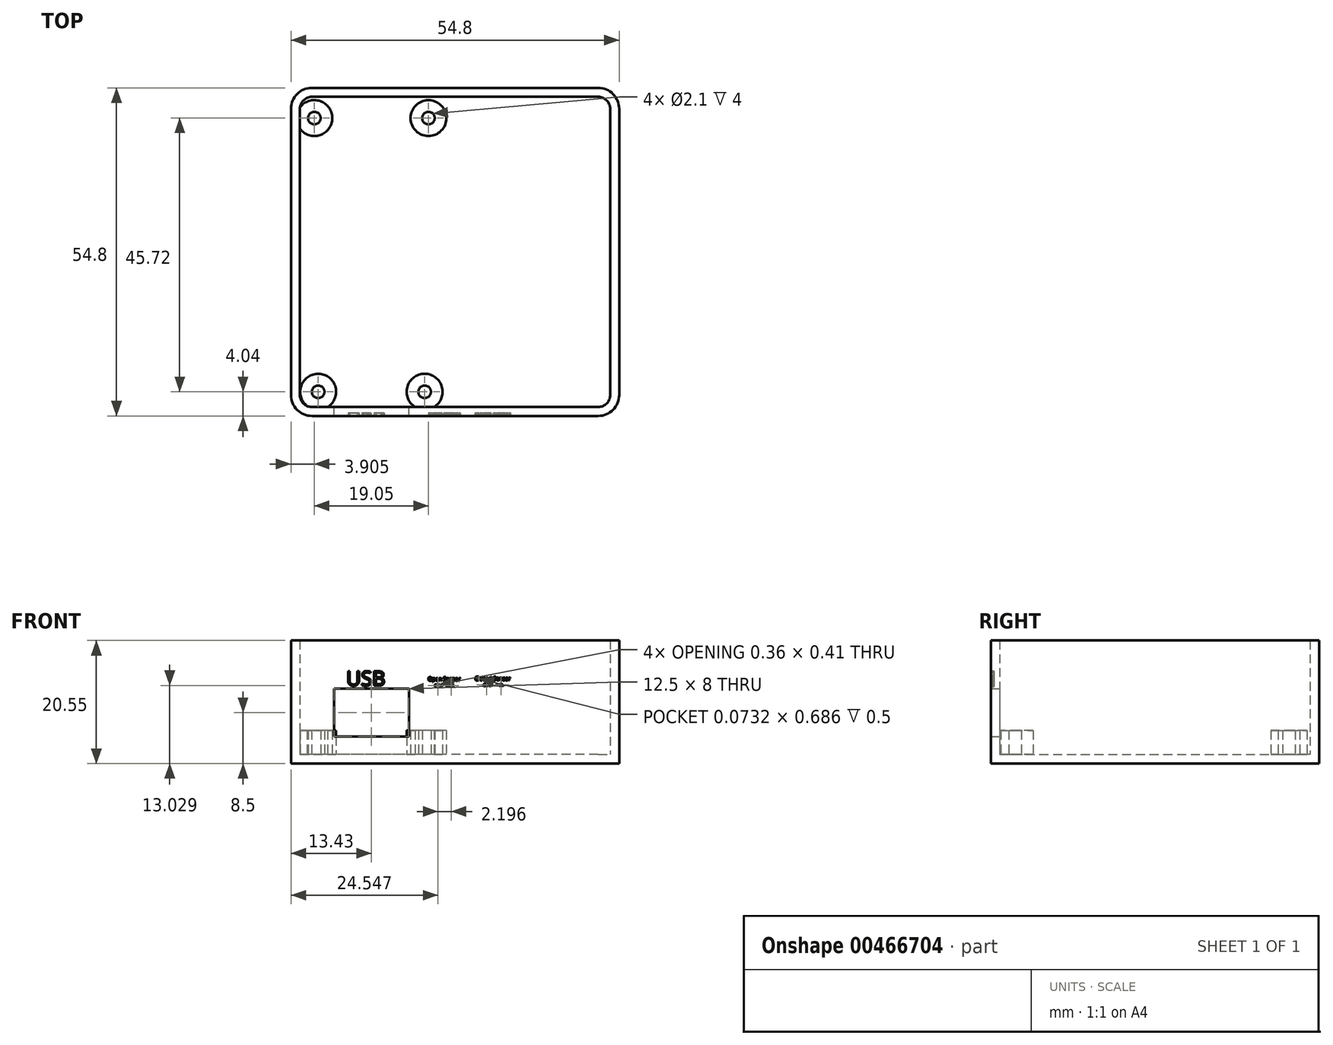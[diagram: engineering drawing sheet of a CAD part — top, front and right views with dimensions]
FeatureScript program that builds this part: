
annotation { "Feature Type Name" : "Feature", "Feature Type Description" : "" }
export const myFeature = defineFeature(function(context is Context, id is Id, definition is map)
    precondition{}
    {
        {
            var Q0;
            Q0=qCreatedBy(makeId("Top.planeOp"),FACE);
            var sketch = newSketch(context, id + "F0", { "sketchPlane" : qUnion([Q0])});
            skLineSegment(sketch, "E0.bottom", {"start": v(23.9, -25.9) * mm, "end": v(-23.9, -25.9) * mm});
            skLineSegment(sketch, "E0.top", {"start": v(23.9, 25.9) * mm, "end": v(-23.9, 25.9) * mm});
            skLineSegment(sketch, "E0.left", {"start": v(25.9, -23.9) * mm, "end": v(25.9, 23.9) * mm});
            skLineSegment(sketch, "E0.right", {"start": v(-25.9, -23.9) * mm, "end": v(-25.9, 23.9) * mm});
            skPoint(sketch, "E0.middle", {"position": v(0, 0) * mm});
            skPoint(sketch, "E1.visualSharp", {"position": v(-25.9, -25.9) * mm});
            skArc(sketch, "E1.filletArc", {"start": v(-25.9, -23.9) * mm, "mid": v(-25.31, -25.31) * mm, "end": v(-23.9, -25.9) * mm});
            skPoint(sketch, "E2.visualSharp", {"position": v(25.9, -25.9) * mm});
            skArc(sketch, "E2.filletArc", {"start": v(23.9, -25.9) * mm, "mid": v(25.31, -25.31) * mm, "end": v(25.9, -23.9) * mm});
            skPoint(sketch, "E3.visualSharp", {"position": v(25.9, 25.9) * mm});
            skArc(sketch, "E3.filletArc", {"start": v(25.9, 23.9) * mm, "mid": v(25.31, 25.31) * mm, "end": v(23.9, 25.9) * mm});
            skPoint(sketch, "E4.visualSharp", {"position": v(-25.9, 25.9) * mm});
            skArc(sketch, "E4.filletArc", {"start": v(-23.9, 25.9) * mm, "mid": v(-25.31, 25.31) * mm, "end": v(-25.9, 23.9) * mm});
            skSolve(sketch);
        }
        {
            var Q0;
            Q0 = qSketchRegion(id + "F0", true);
            extrude(context, id + "F1", {"entities" : qUnion([Q0]), "depth" : 19.05 * mm, "offsetDistance" : 25 * mm});
        }
        {
            var Q0;
            Q0=makeQuery(id+"F1.opExtrude","CAP_FACE",FACE,{"disambiguationData":[OSD([sQuery(id+"F0.wireOp",EDGE,"E0.bottom"),sQuery(id+"F0.wireOp",EDGE,"E0.top"),sQuery(id+"F0.wireOp",EDGE,"E0.left"),sQuery(id+"F0.wireOp",EDGE,"E0.right")])],"isStart":false});
            shell(context, id + "F2", {"entities" : qUnion([Q0]), "thickness" : 1.5 * mm, "oppositeDirection" : true});
        }
        {
            var Q0;
            Q0=makeQuery(id+"F2.opShell","OFFSET_FACE",FACE,{"disambiguationData":[OSD([sQuery(id+"F0.wireOp",EDGE,"E0.bottom"),sQuery(id+"F0.wireOp",EDGE,"E0.top"),sQuery(id+"F0.wireOp",EDGE,"E0.left"),sQuery(id+"F0.wireOp",EDGE,"E0.right")])]});
            var sketch = newSketch(context, id + "F3", { "sketchPlane" : qUnion([Q0])});
            skLineSegment(sketch, "E5.bottom", {"start": v(-23.4, 24.9) * mm, "end": v(-4.54, 24.9) * mm, "construction": true});
            skLineSegment(sketch, "E5.top", {"start": v(-23.4, -25.9) * mm, "end": v(-4.54, -25.9) * mm, "construction": true});
            skLineSegment(sketch, "E5.left", {"start": v(-25.4, 22.9) * mm, "end": v(-25.4, -23.9) * mm});
            skLineSegment(sketch, "E5.right", {"start": v(-2.54, 22.9) * mm, "end": v(-2.54, -23.9) * mm, "construction": true});
            skPoint(sketch, "E5.middle", {"position": v(-13.97, -0.5) * mm});
            skPoint(sketch, "E6.visualSharp", {"position": v(-25.4, 24.9) * mm});
            skArc(sketch, "E6.filletArc", {"start": v(-23.4, 24.9) * mm, "mid": v(-24.81, 24.31) * mm, "end": v(-25.4, 22.9) * mm, "construction": true});
            skPoint(sketch, "E7.visualSharp", {"position": v(-2.54, 24.9) * mm});
            skArc(sketch, "E7.filletArc", {"start": v(-2.54, 22.9) * mm, "mid": v(-3.13, 24.31) * mm, "end": v(-4.54, 24.9) * mm, "construction": true});
            skPoint(sketch, "E8.visualSharp", {"position": v(-2.54, -25.9) * mm});
            skArc(sketch, "E8.filletArc", {"start": v(-4.54, -25.9) * mm, "mid": v(-3.13, -25.31) * mm, "end": v(-2.54, -23.9) * mm, "construction": true});
            skPoint(sketch, "E9.visualSharp", {"position": v(-25.4, -25.9) * mm});
            skArc(sketch, "E9.filletArc", {"start": v(-25.4, -23.9) * mm, "mid": v(-24.81, -25.31) * mm, "end": v(-23.4, -25.9) * mm, "construction": true});
            skCircle(sketch, "E10", {"center": v(-4.44, 22.36) * mm, "radius": 3 * mm});
            skCircle(sketch, "E11", {"center": v(-5.08, -23.36) * mm, "radius": 3 * mm});
            skCircle(sketch, "E12", {"center": v(-22.86, -23.36) * mm, "radius": 3 * mm});
            skCircle(sketch, "E13", {"center": v(-23.5, 22.36) * mm, "radius": 3 * mm});
            skCircle(sketch, "E14", {"center": v(-23.5, 22.36) * mm, "radius": 1.05 * mm});
            skCircle(sketch, "E15", {"center": v(-4.44, 22.36) * mm, "radius": 1.05 * mm});
            skCircle(sketch, "E16", {"center": v(-22.86, -23.36) * mm, "radius": 1.05 * mm});
            skCircle(sketch, "E17", {"center": v(-5.08, -23.36) * mm, "radius": 1.05 * mm});
            skLineSegment(sketch, "E18", {"start": v(-13.97, -0.5) * mm, "end": v(-13.97, -25.9) * mm, "construction": true});
            skSolve(sketch);
        }
        {
            var Q0;
            Q0 = qSketchRegion(id + "F3", true);
            extrude(context, id + "F4", {"entities" : qUnion([Q0]), "operationType" : NewBodyOperationType.ADD, "depth" : 4 * mm, "offsetDistance" : 25 * mm});
        }
        {
            var Q0;
            Q0=makeQuery(id+"F2.opShell","OFFSET_FACE",FACE,{"disambiguationData":[OSD([sQuery(id+"F0.wireOp",EDGE,"E0.bottom")])]});
            var sketch = newSketch(context, id + "F5", { "sketchPlane" : qUnion([Q0])});
            skLineSegment(sketch, "E19.bottom", {"start": v(7.72, 11) * mm, "end": v(20.22, 11) * mm});
            skLineSegment(sketch, "E19.top", {"start": v(7.72, 3) * mm, "end": v(20.22, 3) * mm});
            skLineSegment(sketch, "E19.left", {"start": v(7.72, 11) * mm, "end": v(7.72, 3) * mm});
            skLineSegment(sketch, "E19.right", {"start": v(20.22, 11) * mm, "end": v(20.22, 3) * mm});
            skPoint(sketch, "E19.middle", {"position": v(13.97, 7) * mm});
            skPoint(sketch, "E20", {"position": v(13.97, 0) * mm});
            skSolve(sketch);
        }
        {
            var Q0;
            Q0 = qSketchRegion(id + "F5", true);
            extrude(context, id + "F6", {"entities" : qUnion([Q0]), "operationType" : NewBodyOperationType.REMOVE, "oppositeDirection" : true, "depth" : 1.5 * mm, "offsetDistance" : 25 * mm});
        }
        {
            var Q0;
            Q0=makeQuery(id+"F1.opExtrude","SWEPT_FACE",FACE,{"disambiguationData":[OSD([sQuery(id+"F0.wireOp",EDGE,"E0.bottom")])]});
            var sketch = newSketch(context, id + "F7", { "sketchPlane" : qUnion([Q0])});
            skText(sketch, "E21", { "text": "Closed Sensor", "fontName": "OpenSans-Regular.ttf"});
            skText(sketch, "E22", { "text": "Open Sensor", "fontName": "OpenSans-Regular.ttf"});
            skText(sketch, "E23", { "text": "COM", "fontName": "OpenSans-Regular.ttf"});
            skText(sketch, "E24", { "text": "N.O.", "fontName": "OpenSans-Regular.ttf"});
            skText(sketch, "E25", { "text": "USB", "fontName": "OpenSans-Regular.ttf"});
            skText(sketch, "E26", { "text": "COM", "fontName": "OpenSans-Regular.ttf"});
            skText(sketch, "E27", { "text": "N.O.", "fontName": "OpenSans-Regular.ttf"});
            const initialGuessF7  = {"E21": [0.0033, 0.01237, 1, 0, 0.00065], "E22": [-0.00453, 0.0123, 1, 0, 0.00065], "E23": [-0.00342, 0.01133, 1, 0, 0.0004], "E24": [-0.00144, 0.01133, 1, 0, 0.0004], "E25": [-0.01818, 0.0115, 1, 0, 0.00244], "E26": [0.00472, 0.01141, 1, 0, 0.0004], "E27": [0.0069, 0.01143, 1, 0, 0.0004]};
            skSetInitialGuess(sketch, initialGuessF7);
            skSolve(sketch);
        }
        {
            var Q0;
            Q0 = qSketchRegion(id + "F7", true);
            extrude(context, id + "F8", {"entities" : qUnion([Q0]), "operationType" : NewBodyOperationType.REMOVE, "oppositeDirection" : true, "depth" : .5 * mm, "offsetDistance" : 25 * mm});
        }
    });
